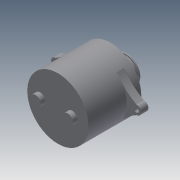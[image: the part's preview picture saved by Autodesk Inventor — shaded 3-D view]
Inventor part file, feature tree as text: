
AUTODESK INVENTOR PART (.ipt)
format: ipt  version: 2015 (Build 190159000, 159)  size: 152,064 bytes
history: native  units: mm
features: extrude x7, sketch x7, projected_geometry x1
ambient origin geometry x8: Origin, YZ Plane, XZ Plane, XY Plane, X Axis, Y Axis, Z Axis, Center Point
bodies: Solid1 (feature_tree)
feature tree (15):
  extrude  "Extrusion1"  Depth=83.82mm TaperAngle=0.0deg
  extrude  "Extrusion2"  Depth=88.773mm
  extrude  "Extrusion3"  Depth=10.0mm
  extrude  "Extrusion4"  Depth=16.256mm TaperAngle=0.0deg
  extrude  "Extrusion5"  Depth=10.0mm
  extrude  "Extrusion6"  Depth=2.921mm TaperAngle=0.0deg
  extrude  "Extrusion7"  Depth=2.921mm
  sketch  "Sketch1"  dims[d0=134.366mm d1=83.82mm d2=0.0mm]
  sketch  "Sketch2"  dims[d3=134.366mm d4=88.773mm]
  sketch  "Sketch3"  dims[d5=20.0mm d6=10.0mm]
  projected_geometry  "Projected Loop1"
  sketch  "Sketch4"  dims[d7=10.0mm d8=16.256mm d9=0.0mm]
  sketch  "Sketch5"  dims[d10=10.0mm d11=0.0mm d12=134.366mm]
  sketch  "Sketch6"  dims[d13=15.875mm d14=0.0mm d15=2.921mm d16=0.0mm]
  sketch  "Sketch7"  dims[d17=60.0mm d18=55.0mm d19=29.21mm d20=0.0mm d21=60.0mm d22=2.921mm d23=0.0mm]
